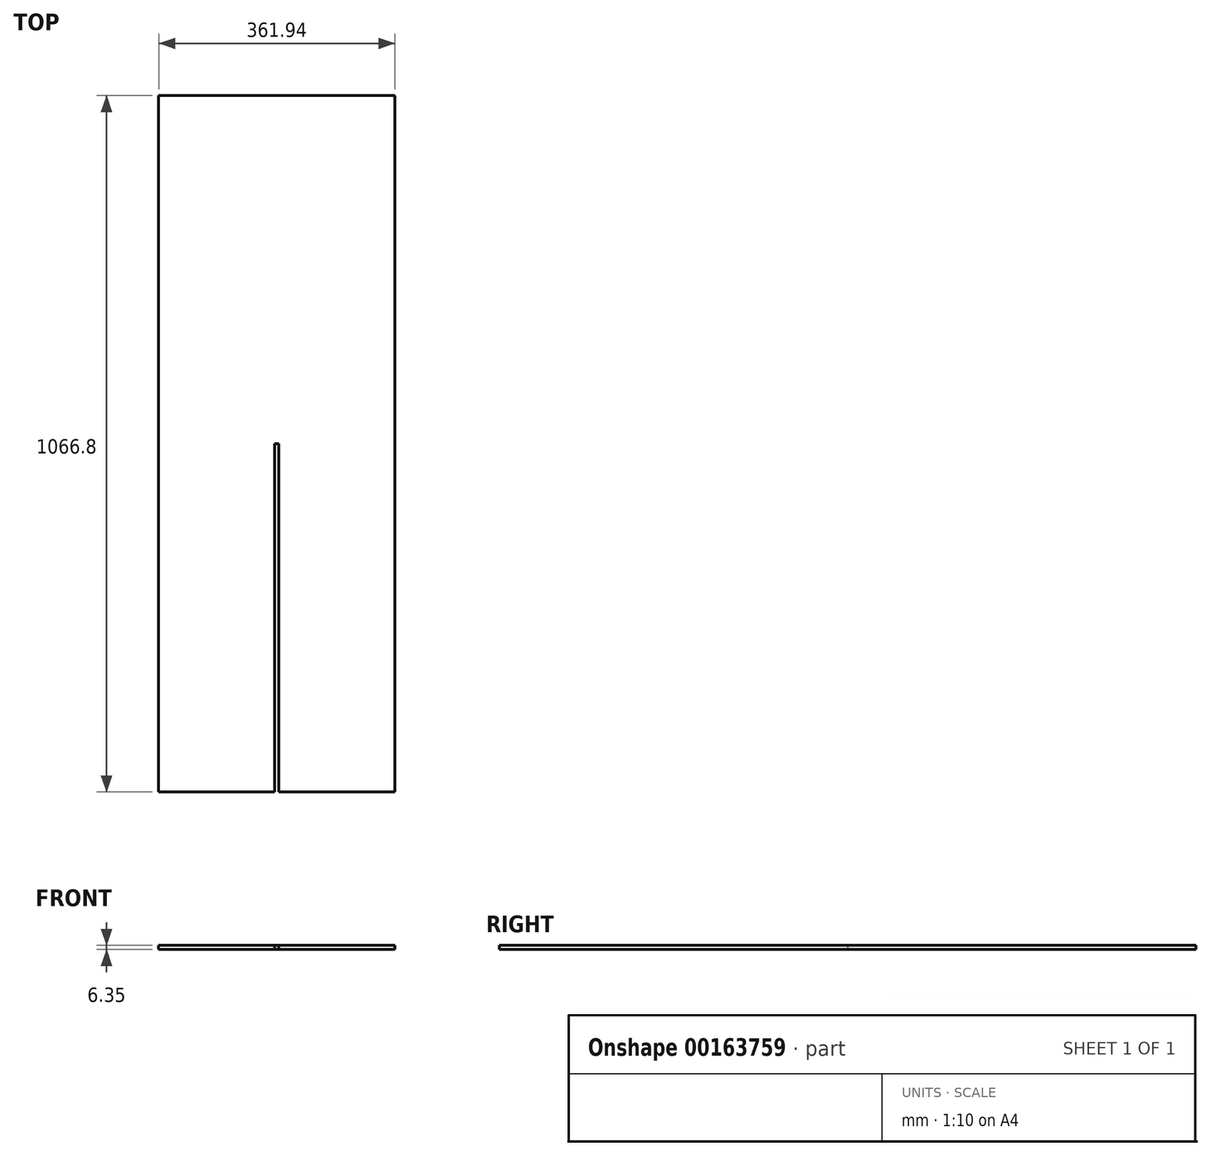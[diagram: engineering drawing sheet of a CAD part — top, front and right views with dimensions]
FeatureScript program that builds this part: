
annotation { "Feature Type Name" : "Feature", "Feature Type Description" : "" }
export const myFeature = defineFeature(function(context is Context, id is Id, definition is map)
    precondition{}
    {
        {
            var Q0;
            Q0=qCreatedBy(makeId("Top.planeOp"),FACE);
            var sketch = newSketch(context, id + "F0", { "sketchPlane" : qUnion([Q0])});
            skLineSegment(sketch, "E0.bottom", {"start": v(180.98, 533.4) * mm, "end": v(-180.97, 533.4) * mm});
            skLineSegment(sketch, "E0.top", {"start": v(180.97, -533.4) * mm, "end": v(3.17, -533.4) * mm});
            skLineSegment(sketch, "E0.left", {"start": v(180.98, 533.4) * mm, "end": v(180.97, -533.4) * mm});
            skLineSegment(sketch, "E0.right", {"start": v(-180.97, 533.4) * mm, "end": v(-180.98, -533.4) * mm});
            skPoint(sketch, "E0.middle", {"position": v(0, 0) * mm});
            skLineSegment(sketch, "E1", {"start": v(0, 0) * mm, "end": v(0, -533.4) * mm, "construction": true});
            skLineSegment(sketch, "E2.0", {"start": v(-3.18, 0) * mm, "end": v(-3.18, -533.4) * mm});
            skLineSegment(sketch, "E3.0", {"start": v(3.17, 0) * mm, "end": v(3.17, -533.4) * mm});
            skLineSegment(sketch, "E4.trimOffspring", {"start": v(-3.18, -533.4) * mm, "end": v(-180.98, -533.4) * mm});
            skLineSegment(sketch, "E5", {"start": v(-3.18, 0) * mm, "end": v(3.17, 0) * mm});
            skSolve(sketch);
        }
        {
            var Q0;
            Q0 = qSketchRegion(id + "F0", true);
            extrude(context, id + "F1", {"entities" : qUnion([Q0]), "depth" : 6.35 * mm, "offsetDistance" : 25.4 * mm});
        }
    });
